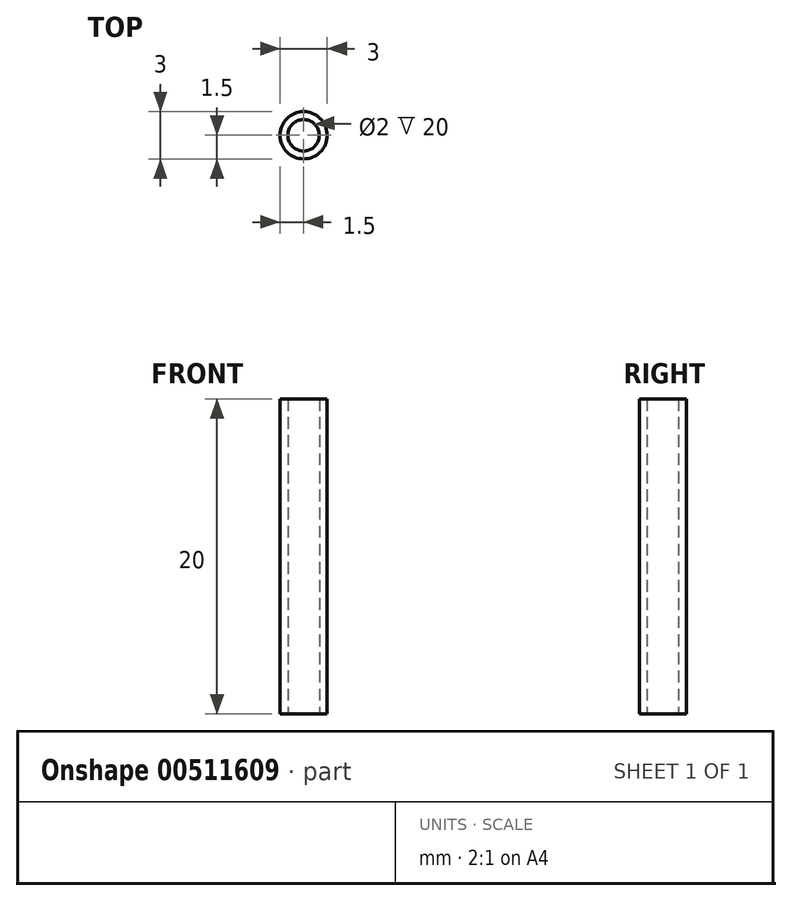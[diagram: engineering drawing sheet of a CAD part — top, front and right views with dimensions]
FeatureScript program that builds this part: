
annotation { "Feature Type Name" : "Feature", "Feature Type Description" : "" }
export const myFeature = defineFeature(function(context is Context, id is Id, definition is map)
    precondition{}
    {
        {
            var Q0;
            Q0=qCreatedBy(makeId("Top.planeOp"),FACE);
            var sketch = newSketch(context, id + "F0", { "sketchPlane" : qUnion([Q0])});
            skCircle(sketch, "E0", {"center": v(0, 0) * mm, "radius": 1.5 * mm});
            skCircle(sketch, "E1", {"center": v(0, 0) * mm, "radius": 0.5 * mm});
            skCircle(sketch, "E2", {"center": v(0, 0) * mm, "radius": 1 * mm});
            skSolve(sketch);
        }
        {
            var Q0;
            Q0=makeQuery(id+"F0.imprint","IMPRINT",FACE,{"disambiguationData":[TD([[makeQuery(id+"F0.imprint","IMPRINT",EDGE,{"derivedFrom":sQuery(id+"F0.wireOp",EDGE,"E0")}),1.0]])]});
            var Q1;
            Q1=makeQuery(id+"F0.imprint","IMPRINT",FACE,{"disambiguationData":[TD([[makeQuery(id+"F0.imprint","IMPRINT",EDGE,{"derivedFrom":sQuery(id+"F0.wireOp",EDGE,"P2dCeyrW-3yyO-GLKp-AFtS-Teg8QAAx5zQA")}),1.0]])]});
            var Q2;
            Q2=makeQuery(id+"F0.imprint","IMPRINT",FACE,{"disambiguationData":[TD([[makeQuery(id+"F0.imprint","IMPRINT",EDGE,{"derivedFrom":sQuery(id+"F0.wireOp",EDGE,"eUsNJooS-I5Mt-Ymv3-55p3-Y8ifr9MI58IP")}),1.0]])]});
            extrude(context, id + "F1", {"entities" : qUnion([Q0, Q1, Q2]), "depth" : 20 * mm});
        }
    });
